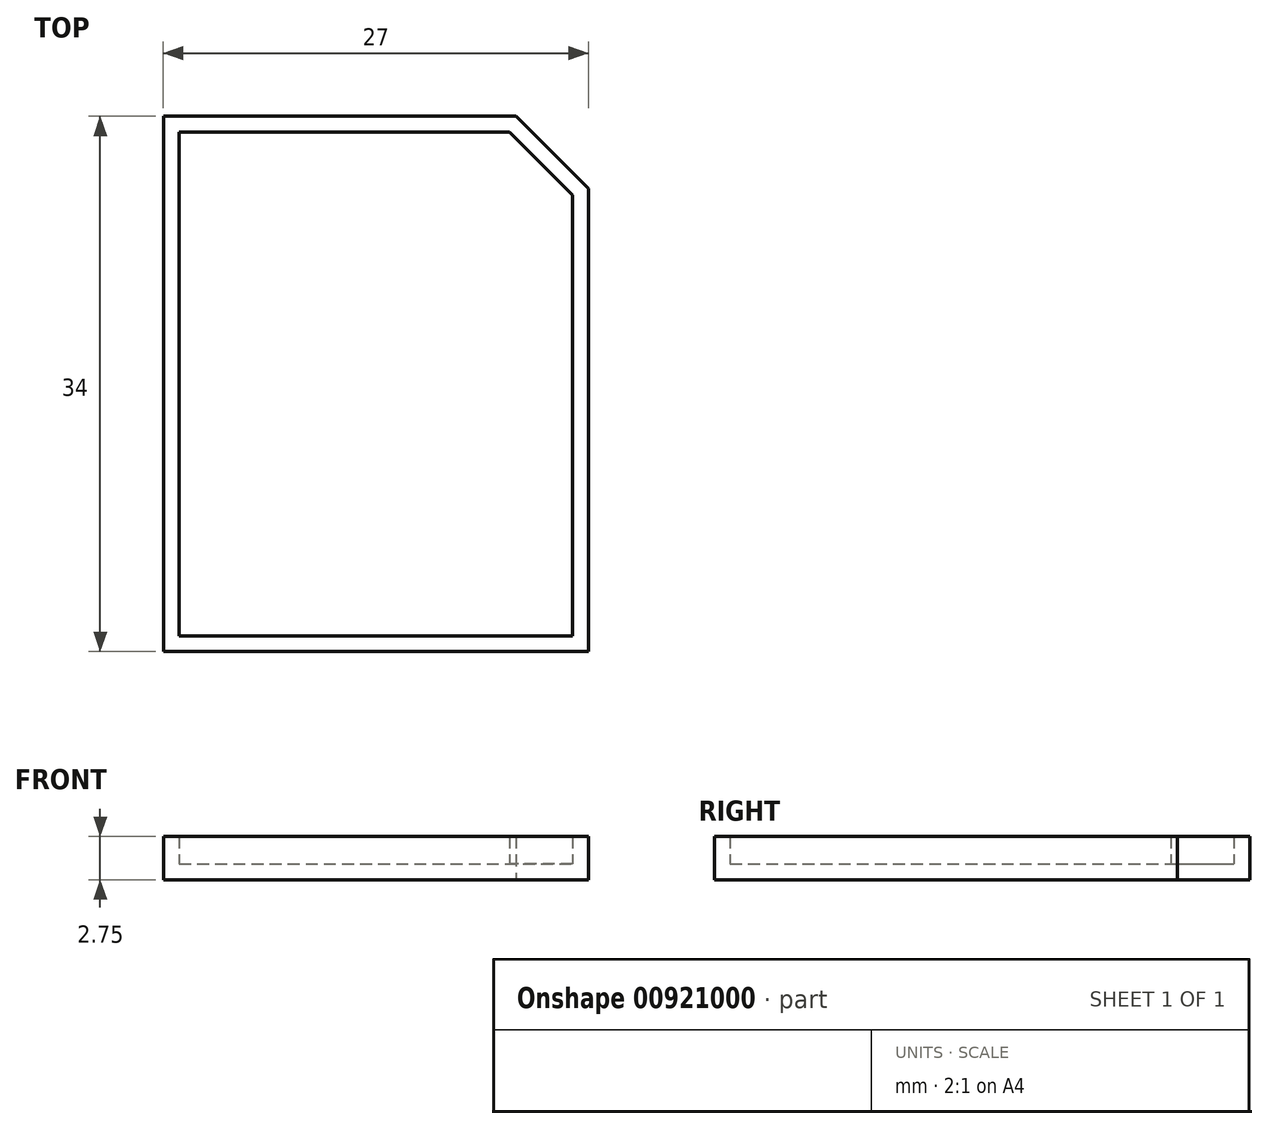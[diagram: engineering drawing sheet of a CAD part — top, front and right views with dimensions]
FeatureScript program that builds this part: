
annotation { "Feature Type Name" : "Feature", "Feature Type Description" : "" }
export const myFeature = defineFeature(function(context is Context, id is Id, definition is map)
    precondition{}
    {
        {
            var Q0;
            Q0=qCreatedBy(makeId("Top.planeOp"),FACE);
            var sketch = newSketch(context, id + "F0", { "sketchPlane" : qUnion([Q0])});
            skLineSegment(sketch, "E0.MirrorCS", {"start": v(39.87, -16) * mm, "end": v(39.87, 16) * mm});
            skLineSegment(sketch, "E1.MirrorCS", {"start": v(39.87, 16) * mm, "end": v(60.87, 16) * mm});
            skPoint(sketch, "E2.MirrorP", {"position": v(64.87, 12) * mm});
            skLineSegment(sketch, "E3.MirrorCS", {"start": v(64.87, 12) * mm, "end": v(60.87, 16) * mm});
            skLineSegment(sketch, "E4.MirrorCS", {"start": v(64.87, -16) * mm, "end": v(64.87, 12) * mm});
            skLineSegment(sketch, "E5.MirrorCS", {"start": v(39.87, -16) * mm, "end": v(64.87, -16) * mm});
            skSolve(sketch);
        }
        {
            var Q0;
            Q0=makeQuery(id+"F0.imprint","IMPRINT",FACE,{"disambiguationData":[TD([[makeQuery(id+"F0.imprint","IMPRINT",EDGE,{"derivedFrom":sQuery(id+"F0.wireOp",EDGE,"E0.MirrorCS")}),-1.0]])]});
            extrude(context, id + "F1", {"entities" : qUnion([Q0]), "depth" : 1.75 * mm, "offsetDistance" : 25 * mm});
        }
        {
            var Q0;
            Q0=makeQuery(id+"F1.opExtrude","CAP_FACE",FACE,{"disambiguationData":[OSD([sQuery(id+"F0.wireOp",EDGE,"E0.MirrorCS"),sQuery(id+"F0.wireOp",EDGE,"E1.MirrorCS"),sQuery(id+"F0.wireOp",EDGE,"E3.MirrorCS"),sQuery(id+"F0.wireOp",EDGE,"E4.MirrorCS"),sQuery(id+"F0.wireOp",EDGE,"E5.MirrorCS")])],"isStart":false});
            shell(context, id + "F2", {"entities" : qUnion([Q0]), "thickness" : 1 * mm, "oppositeDirection" : true});
        }
    });
